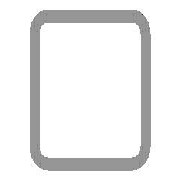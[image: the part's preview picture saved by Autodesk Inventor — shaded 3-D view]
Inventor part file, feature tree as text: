
AUTODESK INVENTOR PART (.ipt)
format: ipt  version: 2025 (Build 290162010, 162A)  size: 132,608 bytes
history: native  units: mm (DEFAULTED — no unit token found)
features: other x4, sketch x1, plane x1
ambient origin geometry x8: Origin, YZ Plane, XZ Plane, XY Plane, X Axis, Y Axis, Z Axis, Center Point
bodies: Solid1 (feature_tree), Body (feature_tree)
feature tree (6):
  parser-record x1  (decoder bookkeeping rows leaked as tree rows — omitted from the tree; the rows remain in map.json)
  other  "Driven Length"
  other  "Start Plane"
  other  "End Plane"
  sketch  "Sketch3"  dims[d3=952.375856mm d4=0.0mm d7=4.0mm d9=40.0mm d11=40.0mm d12=2.0mm d13=-0.0mm d14=952.375856mm d15=20.0mm d16=20.0mm d17=90.0deg d18=952.375856mm]
  plane  "Work Plane3"
